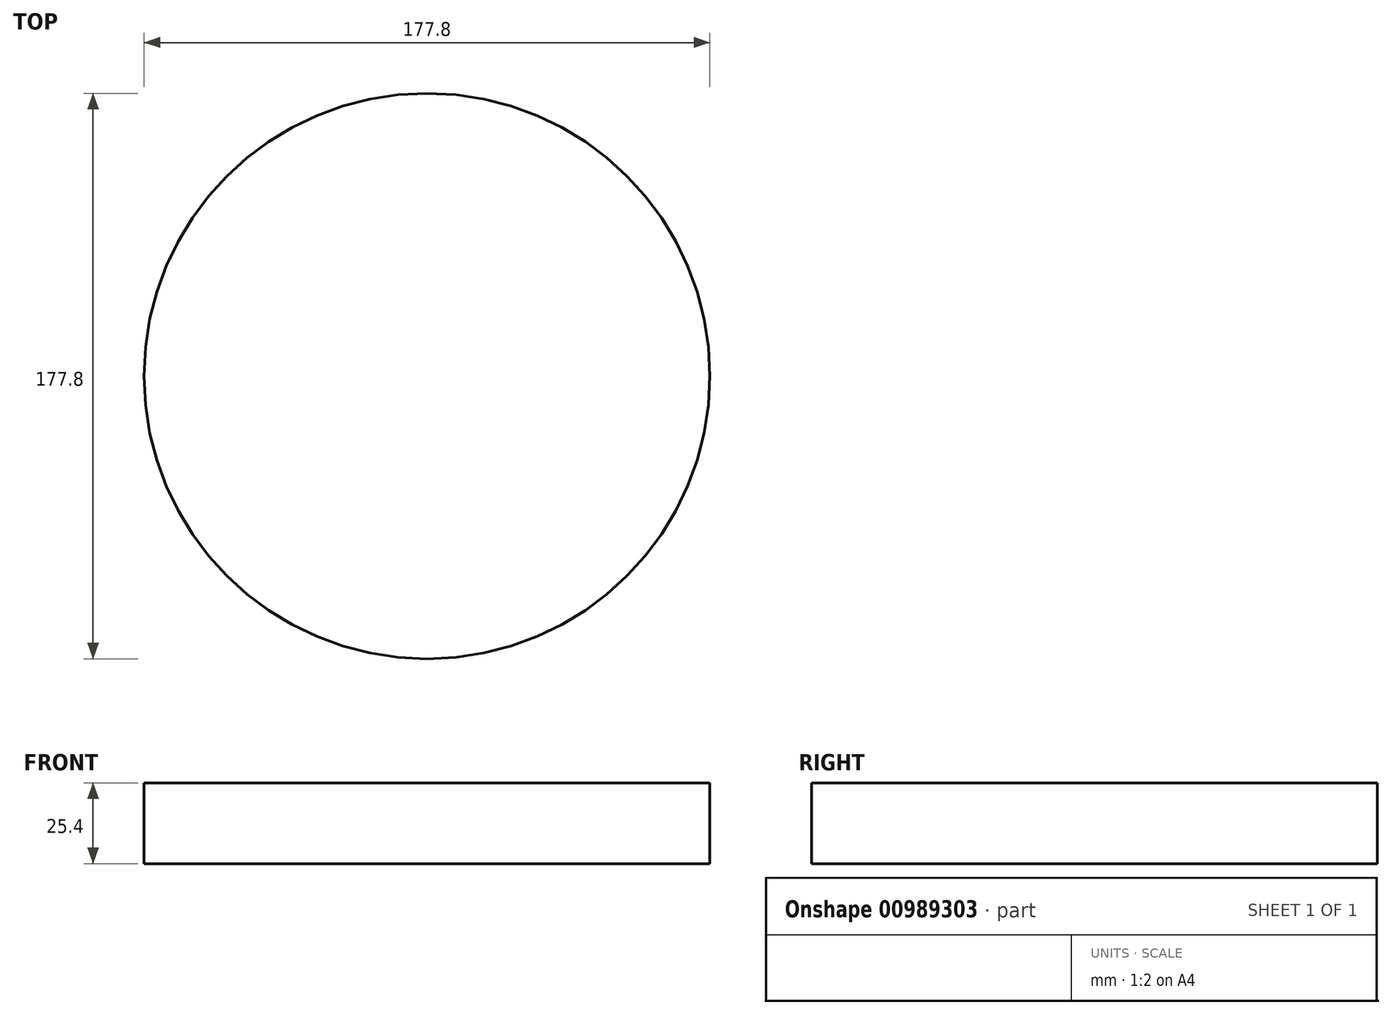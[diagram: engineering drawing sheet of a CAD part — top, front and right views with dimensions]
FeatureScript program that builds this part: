
annotation { "Feature Type Name" : "Feature", "Feature Type Description" : "" }
export const myFeature = defineFeature(function(context is Context, id is Id, definition is map)
    precondition{}
    {
        {
            var Q0;
            Q0=qCreatedBy(makeId("Top.planeOp"),FACE);
            var sketch = newSketch(context, id + "F0", { "sketchPlane" : qUnion([Q0])});
            skCircle(sketch, "E0", {"center": v(0, 0) * mm, "radius": 88.9 * mm});
            skSolve(sketch);
        }
        {
            var Q0;
            Q0 = qSketchRegion(id + "F0", true);
            extrude(context, id + "F1", {"entities" : qUnion([Q0]), "depth" : 25.4 * mm, "offsetDistance" : 25.4 * mm});
        }
    });
